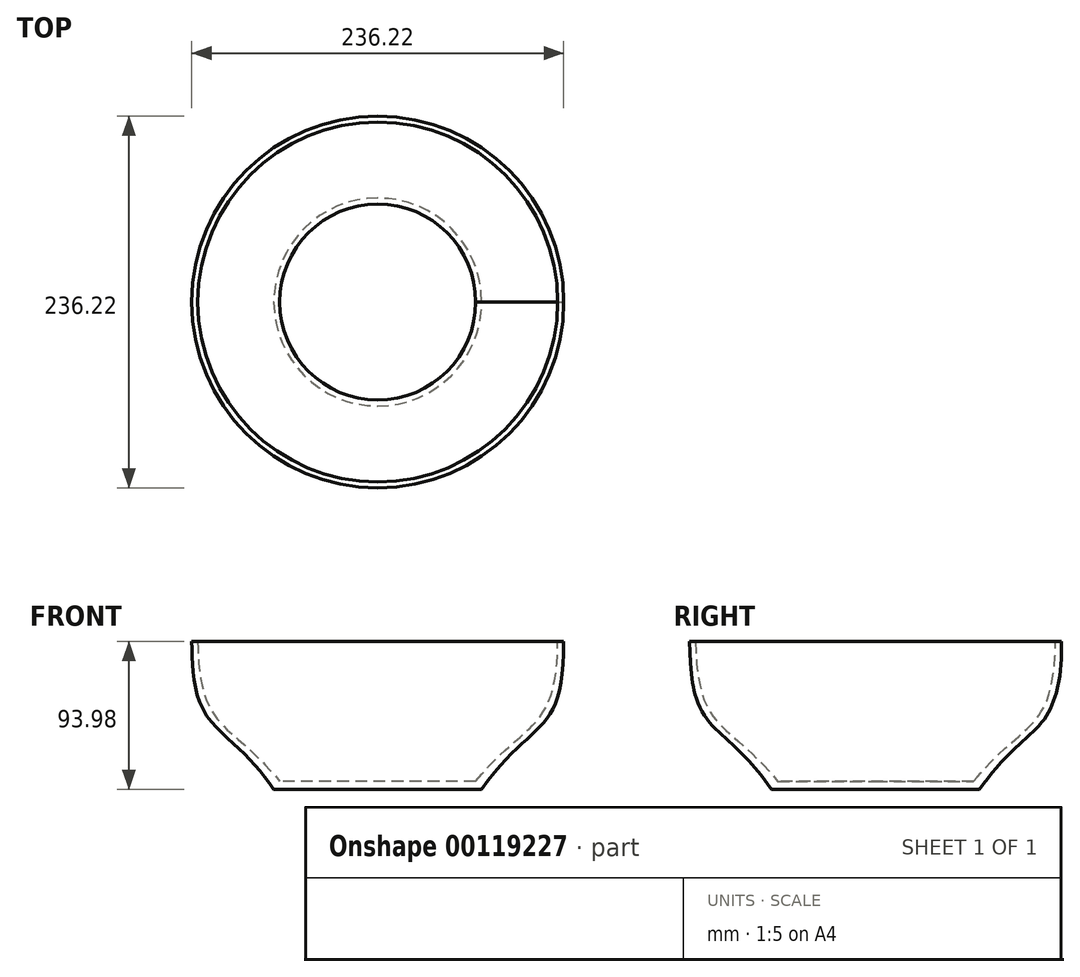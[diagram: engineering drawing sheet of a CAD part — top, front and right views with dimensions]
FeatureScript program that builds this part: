
annotation { "Feature Type Name" : "Feature", "Feature Type Description" : "" }
export const myFeature = defineFeature(function(context is Context, id is Id, definition is map)
    precondition{}
    {
        {
            var Q0;
            Q0=qCreatedBy(makeId("Front.planeOp"),FACE);
            var sketch = newSketch(context, id + "F0", { "sketchPlane" : qUnion([Q0])});
            skLineSegment(sketch, "E0", {"start": v(0, 0) * mm, "end": v(-66.04, 0) * mm});
            skLineSegment(sketch, "E1", {"start": v(0, 0) * mm, "end": v(0, 5.08) * mm});
            skLineSegment(sketch, "E2", {"start": v(0, 5.08) * mm, "end": v(-62.23, 5.08) * mm});
            skFitSpline(sketch, "E3", {"points": [v(-62.23, 5.08) * mm, v(-114.3, 93.98) * mm], "startDerivative": vector(-92.7, 116.08) * mm, "endDerivative": vector(-1.77, 175.78) * mm});
            skFitSpline(sketch, "E4", {"points": [v(-66.04, 0) * mm, v(-118.11, 93.98) * mm], "startDerivative": vector(-95.67, 137.39) * mm, "endDerivative": vector(0, 185.83) * mm});
            skLineSegment(sketch, "E5", {"start": v(-118.11, 93.98) * mm, "end": v(-114.3, 93.98) * mm});
            skLineSegment(sketch, "E6", {"start": v(0, 110.33) * mm, "end": v(0, 71.87) * mm});
            skSolve(sketch);
        }
        {
            var Q0;
            Q0=makeQuery(id+"F0.imprint","IMPRINT",FACE,{"disambiguationData":[TD([[makeQuery(id+"F0.imprint","IMPRINT",EDGE,{"derivedFrom":sQuery(id+"F0.wireOp",EDGE,"E0")}),-1.0]])]});
            var Q1;
            Q1=sQuery(id+"F0.wireOp",EDGE,"E6");
            revolve(context, id + "F1", {"entities" : qUnion([Q0]), "axis" : qUnion([Q1]), "revolveType" : RevolveType.FULL});
        }
    });
